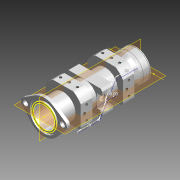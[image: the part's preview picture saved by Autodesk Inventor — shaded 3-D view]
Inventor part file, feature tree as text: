
AUTODESK INVENTOR PART (.ipt)
format: ipt  version: 2015 (Build 190159000, 159)  size: 452,608 bytes
history: native  units: mm
features: sketch x15, projected_geometry x6, extrude x5, hole x5, reference x4, revolve x3, fillet x1, mirror x1
ambient origin geometry x8: Origin, YZ Plane, XZ Plane, XY Plane, X Axis, Y Axis, Z Axis, Center Point
bodies: Solid1 (feature_tree)
feature tree (40):
  revolve  "Revolution1"  [1 undecoded]
  sketch  "Sketch5"  dims[d3=14.0mm d4=120.0mm]
  extrude  "Extrusion2"  Depth=120.0mm
  extrude  "Extrusion3"  Depth=2.0mm
  fillet  "Fillet1"  Radius=1.0mm
  revolve  "Revolution2"  [1 undecoded]
  extrude  "Extrusion4"  TaperAngle=90.0deg  [1 undecoded]
  revolve  "Revolution3"  [1 undecoded]
  extrude  "Extrusion5"  Depth=4.0mm TaperAngle=0.0deg
  extrude  "Extrusion6"  Depth=2.0mm
  hole  "Hole4"  [1 undecoded]
  hole  "Hole5"  [1 undecoded]
  hole  "Hole6"  [1 undecoded]
  sketch  "Sketch17"  dims[d58=20.0mm d59=20.0mm]
  mirror  "Mirror1"
  hole  "Hole7"  [1 undecoded]
  hole  "Hole8"  [1 undecoded]
  sketch  "Sketch1"  dims[d1=13.5mm d2=21.5mm]
  sketch  "Sketch7"  dims[d5=2.0mm d6=0.4mm d7=1.0mm]
  sketch  "Sketch8"  dims[d8=0.4mm d9=1.0mm]
  sketch  "Sketch9"  dims[d10=8.5mm d11=90.0deg]
  sketch  "Sketch10"  dims[d24=6.5mm d27=6.5mm]
  sketch  "Sketch11"  dims[d28=37.0mm d35=4.0mm d36=0.0mm]
  projected_geometry  "Projected Loop2"
  sketch  "Sketch12"  dims[d37=2.0mm d38=0.0mm d39=2.0mm]
  sketch  "Sketch13"  dims[d42=14.0mm d47=10.5mm]
  sketch  "Sketch14"  dims[d49=90.0deg d50=8.0mm]
  projected_geometry  "Projected Loop3"
  sketch  "Sketch15"  dims[d53=8.0mm d54=0.0mm]
  reference  "Reference1"
  reference  "Reference2"
  sketch  "Sketch16"  dims[d55=10.5mm d57=35.0mm]
  reference  "Reference3"
  reference  "Reference4"
  sketch  "Sketch18"  dims[d60=35.0mm]
  projected_geometry  "Projected Loop4"
  projected_geometry  "Projected Loop5"
  sketch  "Sketch19"  dims[d61=10.5mm d62=11.0mm d63=90.0deg d64=7.0mm d65=0.0mm d66=0.0mm d67=0.0mm d68=0.0mm d69=7.0mm d86=4.0mm d87=4.0mm d88=9.0mm d89=9.0mm d90=3.242mm d91=5.0mm d92=4.0mm d93=2.0mm d94=90.0deg d95=6.0mm d96=20.594885mm d97=4.134mm d98=5.0mm d99=4.0mm d100=2.0mm d101=90.0deg d102=7.0mm d103=20.594885mm d104=4.134mm d105=5.0mm d106=4.0mm d107=2.0mm d108=90.0deg d109=7.0mm d110=20.594885mm d113=7.0mm d118=20.0mm d119=60.0deg d120=29.0mm d121=20.0mm d123=29.0mm d124=19.0mm d125=2.0mm d126=2.0mm d127=2.0mm d129=4.0mm d130=6.0mm d131=4.0mm d132=2.0mm d133=90.0deg d134=8.0mm d135=20.594885mm d137=3.242mm d138=8.0mm d139=4.0mm d140=2.0mm d141=90.0deg d142=6.0mm d143=20.594885mm d144=22.0mm d145=22.0mm d146=0.0mm d147=60.0mm d148=3.5mm d149=22.0mm d150=6.0mm d151=6.0mm d152=3.5mm d155=48.0mm d157=24.0mm]
  projected_geometry  "Projected Loop6"
  projected_geometry  "Projected Loop7"
note: 9 required parameter values undecoded (feature->parameter linkage not recoverable at this tier; creation-order binding heuristic only, values carry confidence <= 0.55)